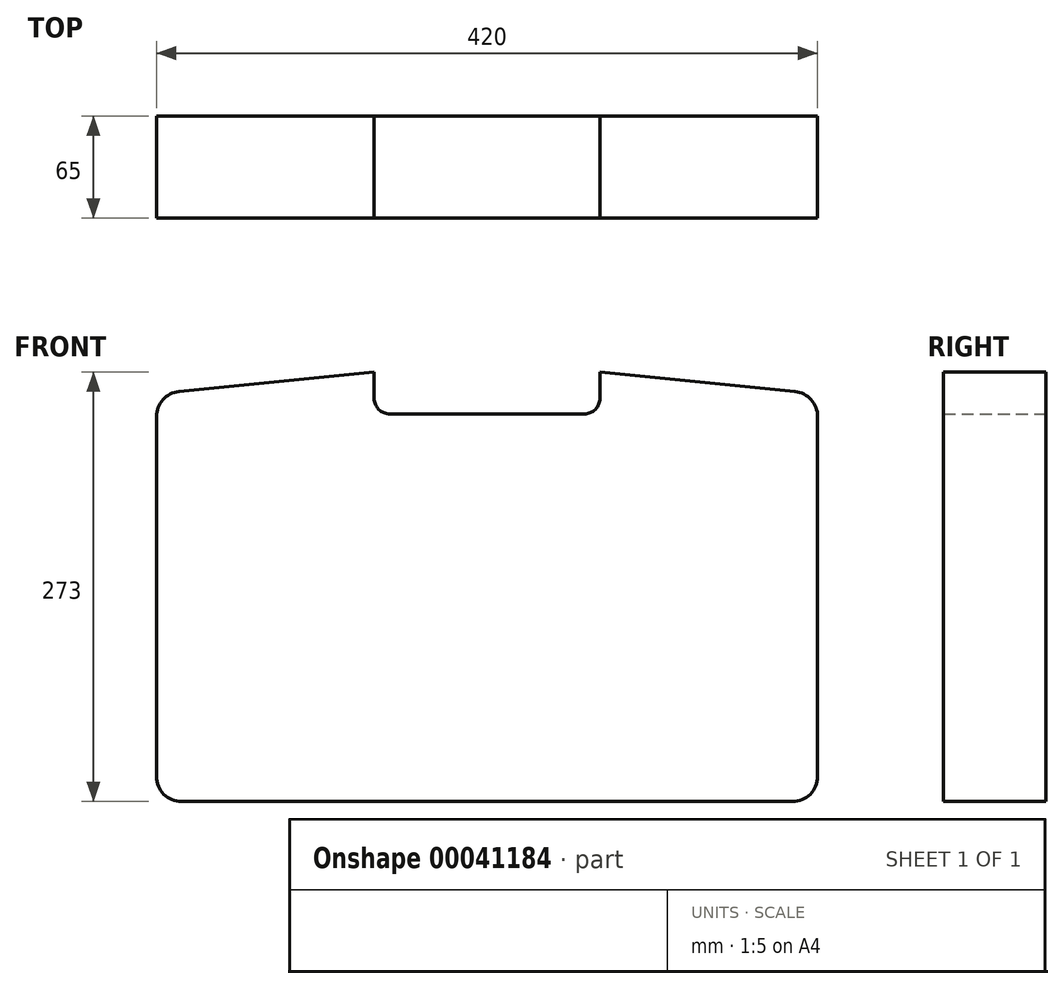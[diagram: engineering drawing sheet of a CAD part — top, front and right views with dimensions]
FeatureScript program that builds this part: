
annotation { "Feature Type Name" : "Feature", "Feature Type Description" : "" }
export const myFeature = defineFeature(function(context is Context, id is Id, definition is map)
    precondition{}
    {
        {
            var Q0;
            Q0=qCreatedBy(makeId("Front.planeOp"),FACE);
            var sketch = newSketch(context, id + "F0", { "sketchPlane" : qUnion([Q0])});
            skLineSegment(sketch, "E0.rect.top", {"start": v(0, -129.5) * mm, "end": v(-194, -129.5) * mm});
            skPoint(sketch, "E0.rect.middle", {"position": v(0, 0) * mm});
            skLineSegment(sketch, "E1", {"start": v(0, -129.5) * mm, "end": v(0, 143.5) * mm, "construction": true});
            skLineSegment(sketch, "E2", {"start": v(0, 143.5) * mm, "end": v(-71.7, 143.5) * mm, "construction": true});
            skLineSegment(sketch, "E3", {"start": v(-71.7, 143.5) * mm, "end": v(-71.7, 126.7) * mm});
            skLineSegment(sketch, "E4", {"start": v(-61.7, 116.7) * mm, "end": v(0, 116.7) * mm});
            skLineSegment(sketch, "E5", {"start": v(-71.7, 143.5) * mm, "end": v(-195.61, 130.96) * mm});
            skLineSegment(sketch, "E6", {"start": v(-210, -113.5) * mm, "end": v(-210, 115.04) * mm});
            skPoint(sketch, "E7", {"position": v(-210, 0) * mm});
            skPoint(sketch, "E8.visualSharp", {"position": v(-210, -129.5) * mm});
            skArc(sketch, "E8.filletArc", {"start": v(-210, -113.5) * mm, "mid": v(-205.31, -124.81) * mm, "end": v(-194, -129.5) * mm});
            skPoint(sketch, "E9.visualSharp", {"position": v(-210, 129.5) * mm});
            skArc(sketch, "E9.filletArc", {"start": v(-195.61, 130.96) * mm, "mid": v(-205.87, 125.77) * mm, "end": v(-210, 115.04) * mm});
            skPoint(sketch, "E10.visualSharp", {"position": v(-71.7, 116.7) * mm});
            skArc(sketch, "E10.filletArc", {"start": v(-71.7, 126.7) * mm, "mid": v(-68.77, 119.63) * mm, "end": v(-61.7, 116.7) * mm});
            skLineSegment(sketch, "E11.MirrorCS", {"start": v(71.7, 143.5) * mm, "end": v(71.7, 126.7) * mm});
            skArc(sketch, "E12.MirrorCS", {"start": v(71.7, 126.7) * mm, "mid": v(68.77, 119.63) * mm, "end": v(61.7, 116.7) * mm});
            skArc(sketch, "E13.MirrorCS", {"start": v(195.61, 130.96) * mm, "mid": v(205.87, 125.77) * mm, "end": v(210, 115.04) * mm});
            skArc(sketch, "E14.MirrorCS", {"start": v(210, -113.5) * mm, "mid": v(205.31, -124.81) * mm, "end": v(194, -129.5) * mm});
            skLineSegment(sketch, "E15.MirrorCS", {"start": v(0, -129.5) * mm, "end": v(194, -129.5) * mm});
            skPoint(sketch, "E16.MirrorP", {"position": v(210, -129.5) * mm});
            skPoint(sketch, "E17.MirrorP", {"position": v(210, 0) * mm});
            skLineSegment(sketch, "E18.MirrorCS", {"start": v(0, 143.5) * mm, "end": v(71.7, 143.5) * mm});
            skPoint(sketch, "E19.MirrorP", {"position": v(210, 129.5) * mm});
            skLineSegment(sketch, "E20.MirrorCS", {"start": v(210, -113.5) * mm, "end": v(210, 115.04) * mm});
            skLineSegment(sketch, "E21.MirrorCS", {"start": v(61.7, 116.7) * mm, "end": v(0, 116.7) * mm});
            skPoint(sketch, "E22.MirrorP", {"position": v(71.7, 116.7) * mm});
            skLineSegment(sketch, "E23.MirrorCS", {"start": v(71.7, 143.5) * mm, "end": v(195.61, 130.96) * mm});
            skSolve(sketch);
        }
        {
            var Q0;
            Q0=makeQuery(id+"F0.imprint","IMPRINT",FACE,{"disambiguationData":[TD([[makeQuery(id+"F0.imprint","IMPRINT",EDGE,{"derivedFrom":sQuery(id+"F0.wireOp",EDGE,"E0.rect.top")}),-1.0]])]});
            extrude(context, id + "F1", {"entities" : qUnion([Q0]), "depth" : 65 * mm});
        }
    });
